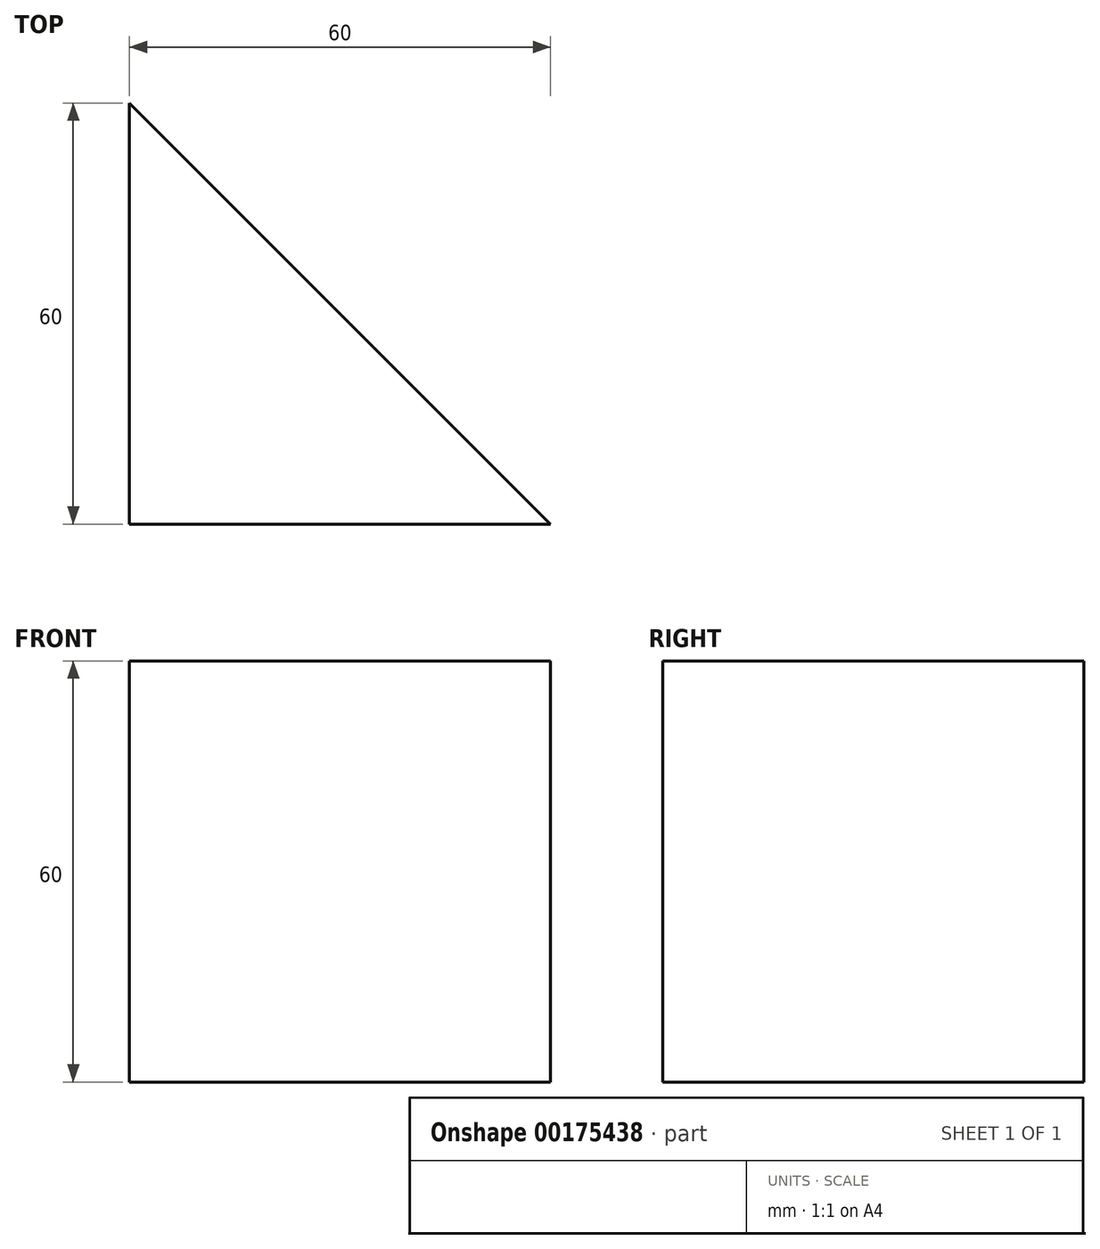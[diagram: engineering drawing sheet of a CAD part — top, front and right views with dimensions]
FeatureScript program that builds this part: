
annotation { "Feature Type Name" : "Feature", "Feature Type Description" : "" }
export const myFeature = defineFeature(function(context is Context, id is Id, definition is map)
    precondition{}
    {
        {
            var Q0;
            Q0=qCreatedBy(makeId("Top.planeOp"),FACE);
            var sketch = newSketch(context, id + "F0", { "sketchPlane" : qUnion([Q0])});
            skPoint(sketch, "E0.0.midPoint", {"position": v(-7.5, -8) * mm});
            skLineSegment(sketch, "E1", {"start": v(-26.24, 45.02) * mm, "end": v(-26.24, -14.98) * mm});
            skLineSegment(sketch, "E2", {"start": v(-26.24, -14.98) * mm, "end": v(33.76, -14.98) * mm});
            skLineSegment(sketch, "E3", {"start": v(-26.24, 45.02) * mm, "end": v(33.76, -14.98) * mm});
            skSolve(sketch);
        }
        {
            var Q0;
            Q0=makeQuery(id+"F0.imprint","IMPRINT",FACE,{"disambiguationData":[TD([[makeQuery(id+"F0.imprint","IMPRINT",EDGE,{"derivedFrom":sQuery(id+"F0.wireOp",EDGE,"E1")}),1.0]])]});
            extrude(context, id + "F1", {"entities" : qUnion([Q0]), "depth" : 60 * mm});
        }
    });
